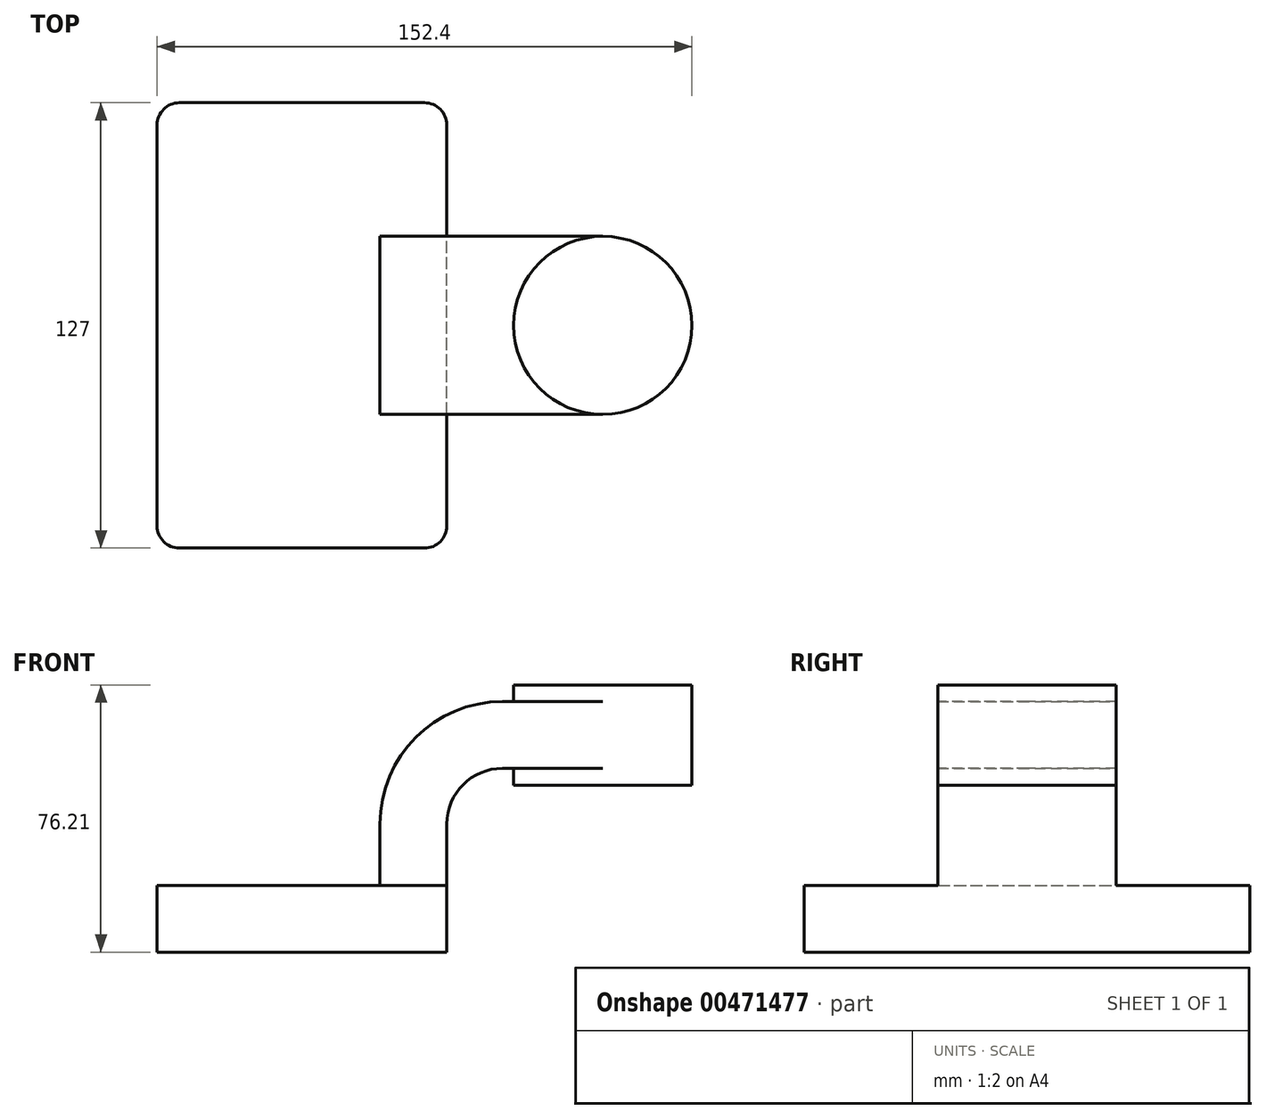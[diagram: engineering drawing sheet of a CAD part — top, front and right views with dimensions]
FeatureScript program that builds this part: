
annotation { "Feature Type Name" : "Feature", "Feature Type Description" : "" }
export const myFeature = defineFeature(function(context is Context, id is Id, definition is map)
    precondition{}
    {
        {
            var Q0;
            Q0=qCreatedBy(makeId("Front.planeOp"),FACE);
            var sketch = newSketch(context, id + "F0", { "sketchPlane" : qUnion([Q0])});
            skLineSegment(sketch, "E0.bottom", {"start": v(-41.28, 9.52) * mm, "end": v(41.27, 9.53) * mm});
            skLineSegment(sketch, "E0.top", {"start": v(-41.27, -9.53) * mm, "end": v(41.28, -9.53) * mm});
            skLineSegment(sketch, "E0.left", {"start": v(-41.28, 9.52) * mm, "end": v(-41.27, -9.53) * mm});
            skLineSegment(sketch, "E0.right", {"start": v(41.28, 9.53) * mm, "end": v(41.28, -9.52) * mm});
            skPoint(sketch, "E0.middle", {"position": v(0, 0) * mm});
            skLineSegment(sketch, "E1.bottom", {"start": v(111.12, 38.1) * mm, "end": v(60.33, 38.1) * mm});
            skLineSegment(sketch, "E1.top", {"start": v(111.12, 66.68) * mm, "end": v(60.32, 66.68) * mm});
            skLineSegment(sketch, "E1.left", {"start": v(111.13, 38.1) * mm, "end": v(111.13, 66.68) * mm});
            skLineSegment(sketch, "E1.right", {"start": v(60.33, 38.1) * mm, "end": v(60.33, 66.68) * mm});
            skPoint(sketch, "E1.middle", {"position": v(85.72, 52.39) * mm});
            skLineSegment(sketch, "E2", {"start": v(41.27, 9.53) * mm, "end": v(41.27, 27) * mm});
            skArc(sketch, "E3", {"start": v(41.27, 27) * mm, "mid": v(45.92, 38.23) * mm, "end": v(57.15, 42.88) * mm});
            skLineSegment(sketch, "E4", {"start": v(57.15, 42.88) * mm, "end": v(85.72, 42.88) * mm});
            skPoint(sketch, "E5", {"position": v(85.72, 38.1) * mm});
            skLineSegment(sketch, "E6.0", {"start": v(57.15, 61.93) * mm, "end": v(85.72, 61.93) * mm});
            skArc(sketch, "E6.1", {"start": v(22.23, 27) * mm, "mid": v(32.45, 51.7) * mm, "end": v(57.15, 61.93) * mm});
            skLineSegment(sketch, "E6.2", {"start": v(22.22, 9.53) * mm, "end": v(22.22, 27) * mm});
            skFitSpline(sketch, "E7", {"points": [v(-41.28, 9.52) * mm, v(57.15, 61.93) * mm], "startDerivative": vector(0.66, 121.97) * mm, "endDerivative": vector(128.95, -5.89) * mm});
            skLineSegment(sketch, "E8", {"start": v(85.72, 38.1) * mm, "end": v(85.72, 66.68) * mm});
            skSolve(sketch);
        }
        {
            var Q0;
            Q0=makeQuery(id+"F0.imprint","IMPRINT",FACE,{"disambiguationData":[TD([[makeQuery(id+"F0.imprint","IMPRINT",EDGE,{"derivedFrom":sQuery(id+"F0.wireOp",EDGE,"E0.top")}),1.0]])]});
            extrude(context, id + "F1", {"entities" : qUnion([Q0]), "endBound" : BoundingType.SYMMETRIC, "depth" : 127 * mm});
        }
        {
            var Q0;
            Q0=makeQuery(id+"F0.imprint","IMPRINT",FACE,{"disambiguationData":[TD([[makeQuery(id+"F0.imprint","IMPRINT",EDGE,{"derivedFrom":sQuery(id+"F0.wireOp",EDGE,"E6.1")}),1.0]])]});
            extrude(context, id + "F2", {"entities" : qUnion([Q0]), "operationType" : NewBodyOperationType.ADD, "endBound" : BoundingType.SYMMETRIC, "depth" : 15.88 * mm});
        }
        {
            var Q0;
            {var subQ1=sQuery(id+"F0.wireOp",EDGE,"E2");Q0=makeQuery(id+"F0.imprint","IMPRINT",FACE,{"disambiguationData":[TD([[makeQuery(id+"F0.imprint","IMPRINT",EDGE,{"derivedFrom":subQ1}),1.0]])]});}
            extrude(context, id + "F3", {"entities" : qUnion([Q0]), "operationType" : NewBodyOperationType.ADD, "endBound" : BoundingType.SYMMETRIC, "depth" : 50.8 * mm});
        }
        {
            var Q0;
            {var subQ0=sQuery(id+"F0.wireOp",EDGE,"E4");var subQ1=sQuery(id+"F0.wireOp",EDGE,"E1.right");var subQ2=makeQuery(id+"F0.imprint","INTERSECT",VERTEX,{"derivedFrom":[subQ1,subQ0]});Q0=makeQuery(id+"F0.imprint","IMPRINT",FACE,{"disambiguationData":[TD([[makeQuery(id+"F0.imprint","IMPRINT",EDGE,{"disambiguationData":[TD([[subQ2,-1.0]])],"derivedFrom":subQ1}),-1.0]])]});}
            extrude(context, id + "F4", {"entities" : qUnion([Q0]), "operationType" : NewBodyOperationType.ADD, "endBound" : BoundingType.SYMMETRIC, "depth" : 50.8 * mm});
        }
        {
            var Q0;
            {var subQ0=sQuery(id+"F0.wireOp",EDGE,"E1.left");Q0=makeQuery(id+"F0.imprint","IMPRINT",FACE,{"disambiguationData":[TD([[makeQuery(id+"F0.imprint","IMPRINT",EDGE,{"derivedFrom":subQ0}),1.0]])]});}
            var Q1;
            Q1=sQuery(id+"F0.wireOp",EDGE,"E8");
            revolve(context, id + "F5", {"operationType" : NewBodyOperationType.ADD, "entities" : qUnion([Q0]), "axis" : qUnion([Q1]), "revolveType" : RevolveType.FULL});
        }
        {
            var Q0;
            Q0=makeQuery(id+"F1.opExtrude","CAP_EDGE",EDGE,{"disambiguationData":[OSD([sQuery(id+"F0.wireOp",EDGE,"E0.left")])],"isStart":false});
            fillet(context, id + "F6", {"entities" : qUnion([Q0]), "radius" : 6.35 * mm, "tangentPropagation" : true, "allowEdgeOverflow" : false});
        }
        {
            var Q0;
            Q0=makeQuery(id+"F1.opExtrude","CAP_EDGE",EDGE,{"disambiguationData":[OSD([sQuery(id+"F0.wireOp",EDGE,"E0.right")])],"isStart":false});
            fillet(context, id + "F7", {"entities" : qUnion([Q0]), "radius" : 6.35 * mm, "tangentPropagation" : true, "allowEdgeOverflow" : false});
        }
        {
            var Q0;
            Q0=makeQuery(id+"F1.opExtrude","CAP_EDGE",EDGE,{"disambiguationData":[OSD([sQuery(id+"F0.wireOp",EDGE,"E0.right")])],"isStart":true});
            fillet(context, id + "F8", {"entities" : qUnion([Q0]), "radius" : 6.35 * mm, "tangentPropagation" : true, "allowEdgeOverflow" : false});
        }
        {
            var Q0;
            Q0=makeQuery(id+"F1.opExtrude","CAP_EDGE",EDGE,{"disambiguationData":[OSD([sQuery(id+"F0.wireOp",EDGE,"E0.left")])],"isStart":true});
            fillet(context, id + "F9", {"entities" : qUnion([Q0]), "radius" : 6.35 * mm, "tangentPropagation" : true, "allowEdgeOverflow" : false});
        }
    });
